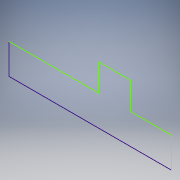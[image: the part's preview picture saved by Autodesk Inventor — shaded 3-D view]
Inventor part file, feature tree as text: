
AUTODESK INVENTOR PART (.ipt)
format: ipt  version: 2016 (Build 200138000, 138)  size: 80,896 bytes
history: native  units: in
note: dims shown in document units (in); Inventor stores cm internally (conversion verified against a paired STEP export)
features: sketch x1
ambient origin geometry x8: Origin, YZ Plane, XZ Plane, XY Plane, X Axis, Y Axis, Z Axis, Center Point
feature tree (1):
  sketch  "Sketch1"
